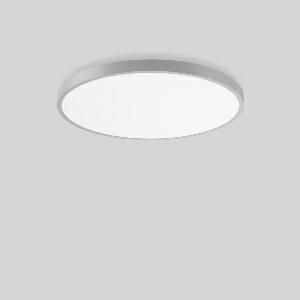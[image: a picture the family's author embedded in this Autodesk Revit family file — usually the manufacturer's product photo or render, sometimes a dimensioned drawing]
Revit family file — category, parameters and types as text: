
# Revit family: triona_round_a_312388_004_2_76_f7d9
name_source: partatom
category: Lighting Fixtures
units: mm (PartAtom-declared; Revit-internal decimal feet)

## family parameters
Cut with Voids When Loaded = No
Host = Face
Light Source = No
Part Type = Normal
Room Calculation Point = No
Round Connector Dimension = Use Diameter
Shared = No

## types (1)
- TuneableWhite 846 (1 x LED Modul 846, 6800 lm, 4600)
    Apparent Load = 76 VA
    CIE Flux Codes = 50 80 96 73 100
    Color Rendering = 80
    Color Temperature = 4600
    Default Elevation = 1800 mm
    Description = Series: TRIONA round
Decorative round LED surface-mounted luminaire. Flat, seamless frame: aluminium extrusion profile, powder coated. Cover made of sheet steel, powder-coated. Direct light emission through a diffuser plastic opal. Indirect light emission through a flush diffuser made of satin-finish plastic. Lightguide and diffuser made of non-yellowing plastic (PMMA). Lateral light emission (RZB SIDELITE technology) for above-average homogeneous light distribution. Direct 70%, indirect 30% light emission. Tunable white versions, dynamically adjustable from 2700 K to 6500 K. Suitable for Ceiling mounting, Wall (surface). Tool-free mounting via bayonet connection. Electronic ballast included. Very easy installation thanks to Plug+Play connection. Ideal for use as part of the Human Centric Lighting concept in connection with RZB light management systems. 
Colour: silver, matt (approx. RAL 9006)
Diameter: 845 mm
Height: 88 mm
Lamp: LED
Socket: without socket
Colour temperature: 2700K - 6500K
Colour rendering index (CRI): 80
System power: 76 W
Rated luminous flux: 6800 lm
Luminous efficiency: 89 lm/W
System power 2: 78 W
Rated luminous flux 2: 6550 lm
Luminous efficiency 2: 84 lm/W
System power 3: 78 W
Rated luminous flux 3: 6550 lm
Luminous efficiency 3: 84 lm/W
Control gear: Converter, dimmable, DALI
Protection class: I
Type of protection: IP 20
    Height = 88 mm
    Lamp = 1 x LED Modul 846
    Lamp Light Flux = 6800 lm
    Lamp count = 1
    Length = 845 mm
    Lifetime = 50000 h
    Luminous efficacy = 89 lm/W
    Manufacturer = RZB
    ModVariant = No
    Model = 312388.004.2.76
    Mounting Place = Ceiling
    Mounting Type = Surface mounted
    Number of Poles = 1
    OnlyDefault = Yes
    Power Factor = 1
    Product Name = TRIONA round A
    Product group = Surface mounted modular luminaires
    ProductGroupID = 306
    Protection Class = Protection class I
    Protection Degree = IP 20
    RLX_Detail_Level = 1
    RLX_Emergency_Light_Flux = 0 lm
    RLX_Emergency_Type = 0
    RLX_Emergency_Type_DB = No
    RlxData = <blob elided: 42429 chars, md5=e2378bbf>
    Socket = socket
    Standby Power = 0 W
    System Light Flux = 6800 lm
    System Power = 76 W
    Type Comments = TuneableWhite 846
    Type Image = 312388.004.jpg
    URL = http://relux.com
    VarID = tuneablewhite_846
    Voltage = 230 V
    Voltage Range = 220-240 V
    Weight = 0.00 kg
    Width = 0 mm  [stored 0 ft]

note: [stored X ft] marks values corroborated as IEEE doubles in the binary element streams (Revit-internal decimal feet)

## geometry (parser evidence)
native form markers: Blend x4, Sweep x12
no freeform markers — native parametric forms only
